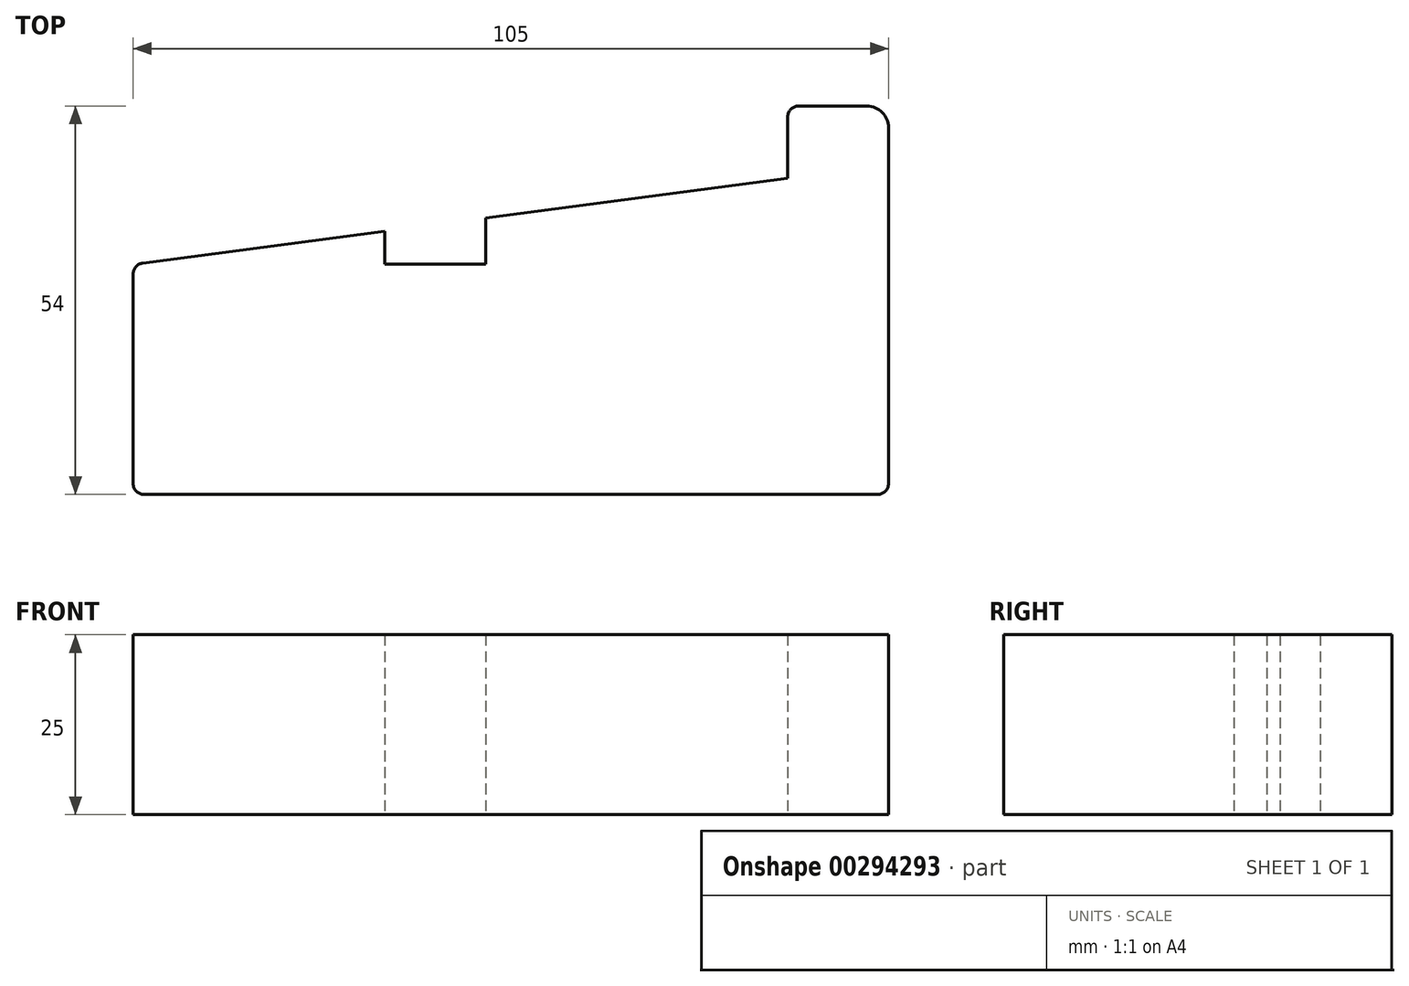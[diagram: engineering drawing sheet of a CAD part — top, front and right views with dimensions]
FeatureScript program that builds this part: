
annotation { "Feature Type Name" : "Feature", "Feature Type Description" : "" }
export const myFeature = defineFeature(function(context is Context, id is Id, definition is map)
    precondition{}
    {
        {
            var Q0;
            Q0=qCreatedBy(makeId("Top.planeOp"),FACE);
            var sketch = newSketch(context, id + "F0", { "sketchPlane" : qUnion([Q0])});
            skLineSegment(sketch, "E0", {"start": v(92.4, -37.35) * mm, "end": v(-12.6, -37.35) * mm});
            skLineSegment(sketch, "E1", {"start": v(-12.6, -35.85) * mm, "end": v(-12.6, -6.67) * mm});
            skLineSegment(sketch, "E2", {"start": v(90.9, -37.35) * mm, "end": v(78.4, -37.35) * mm});
            skLineSegment(sketch, "E3", {"start": v(78.4, 6.65) * mm, "end": v(36.4, 1.1) * mm});
            skLineSegment(sketch, "E4", {"start": v(78.4, 6.65) * mm, "end": v(78.4, 15.15) * mm});
            skLineSegment(sketch, "E5", {"start": v(79.9, 16.65) * mm, "end": v(89.4, 16.65) * mm});
            skLineSegment(sketch, "E6", {"start": v(92.4, 13.65) * mm, "end": v(92.4, -35.85) * mm});
            skLineSegment(sketch, "E7", {"start": v(-11.1, -37.35) * mm, "end": v(22.4, -37.35) * mm});
            skLineSegment(sketch, "E8", {"start": v(22.4, -37.35) * mm, "end": v(36.4, -37.35) * mm});
            skLineSegment(sketch, "E9", {"start": v(36.4, -37.35) * mm, "end": v(36.4, -5.35) * mm});
            skLineSegment(sketch, "E10", {"start": v(36.4, -5.35) * mm, "end": v(22.4, -5.35) * mm});
            skLineSegment(sketch, "E11", {"start": v(22.4, -5.35) * mm, "end": v(22.4, -0.74) * mm});
            skLineSegment(sketch, "E12", {"start": v(36.4, -5.35) * mm, "end": v(36.4, 1.1) * mm});
            skLineSegment(sketch, "E13.trimOffspring", {"start": v(22.4, -0.74) * mm, "end": v(-11.3, -5.18) * mm});
            skPoint(sketch, "E14.visualSharp", {"position": v(-12.6, -37.35) * mm});
            skArc(sketch, "E14.filletArc", {"start": v(-12.6, -35.85) * mm, "mid": v(-12.17, -36.91) * mm, "end": v(-11.1, -37.35) * mm});
            skPoint(sketch, "E15.visualSharp", {"position": v(-12.6, -5.35) * mm});
            skArc(sketch, "E15.filletArc", {"start": v(-11.3, -5.18) * mm, "mid": v(-12.24, -5.68) * mm, "end": v(-12.6, -6.67) * mm});
            skPoint(sketch, "E16.visualSharp", {"position": v(92.4, -37.35) * mm});
            skArc(sketch, "E16.filletArc", {"start": v(90.9, -37.35) * mm, "mid": v(91.95, -36.91) * mm, "end": v(92.4, -35.85) * mm});
            skPoint(sketch, "E17.visualSharp", {"position": v(78.4, 16.65) * mm});
            skArc(sketch, "E17.filletArc", {"start": v(79.9, 16.65) * mm, "mid": v(78.83, 16.2) * mm, "end": v(78.4, 15.15) * mm});
            skPoint(sketch, "E18.visualSharp", {"position": v(92.4, 16.65) * mm});
            skArc(sketch, "E18.filletArc", {"start": v(92.4, 13.65) * mm, "mid": v(91.51, 15.77) * mm, "end": v(89.4, 16.65) * mm});
            skSolve(sketch);
        }
        {
            var Q0;
            Q0 = qSketchRegion(id + "F0", true);
            extrude(context, id + "F1", {"entities" : qUnion([Q0]), "depth" : 25 * mm});
        }
    });
